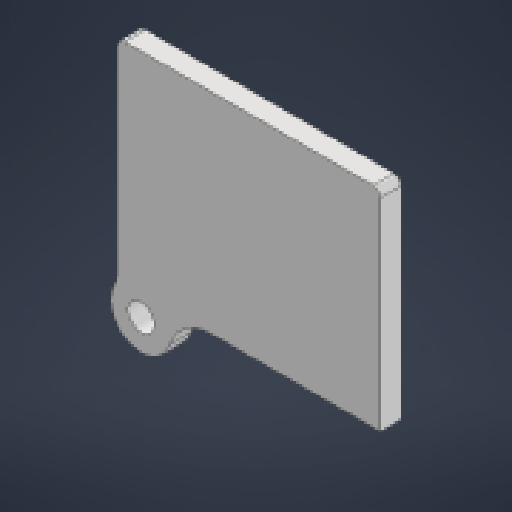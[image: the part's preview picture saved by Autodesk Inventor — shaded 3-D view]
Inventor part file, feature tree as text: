
AUTODESK INVENTOR PART (.ipt)
format: ipt  version: 2025 (Build 290162000, 162)  size: 171,008 bytes
history: native  units: mm
features: other x9, extrude x3, fillet x3, sketch x3, reference x2
ambient origin geometry x8: Origin, YZ Plane, XZ Plane, XY Plane, X Axis, Y Axis, Z Axis, Center Point
bodies: Body1 (feature_tree)
feature tree (20):
  extrude  "拉伸2"  Depth=0.8mm TaperAngle=0.0deg
  extrude  "拉伸3"  Depth=5.0mm TaperAngle=0.0deg
  other  "直接编辑1"
  fillet  "圆角1"  Radius=8.0mm
  fillet  "圆角2"  Radius=2.0mm
  other  "直接编辑2"
  other  "直接编辑3"
  extrude  "拉伸4"  Depth=12.0mm TaperAngle=0.0deg
  fillet  "圆角3"  Radius=12.0mm
  sketch  "草图1"  dims[d2=3.0mm d3=0.8mm d4=0.0mm]
  reference  "参考1"
  sketch  "草图2"  dims[d5=3.0mm d6=5.0mm d7=0.0mm d8=8.0mm d9=2.0mm]
  reference  "参考2"
  sketch  "草图3"  dims[d10=0.0mm d11=0.0mm d12=-3.25mm d14=8.5mm d15=0.0mm d16=12.0mm d17=7.3mm]
  parser-record x1  (decoder bookkeeping rows leaked as tree rows — omitted from the tree; the rows remain in map.json)
  other  "部件1.iam"
  other  "键盘:1"
  other  "删除1"
  other  "移动1"
  other  "删除2"
note: 1 file-system path scrubbed to <path> (originals preserved in map.json)
